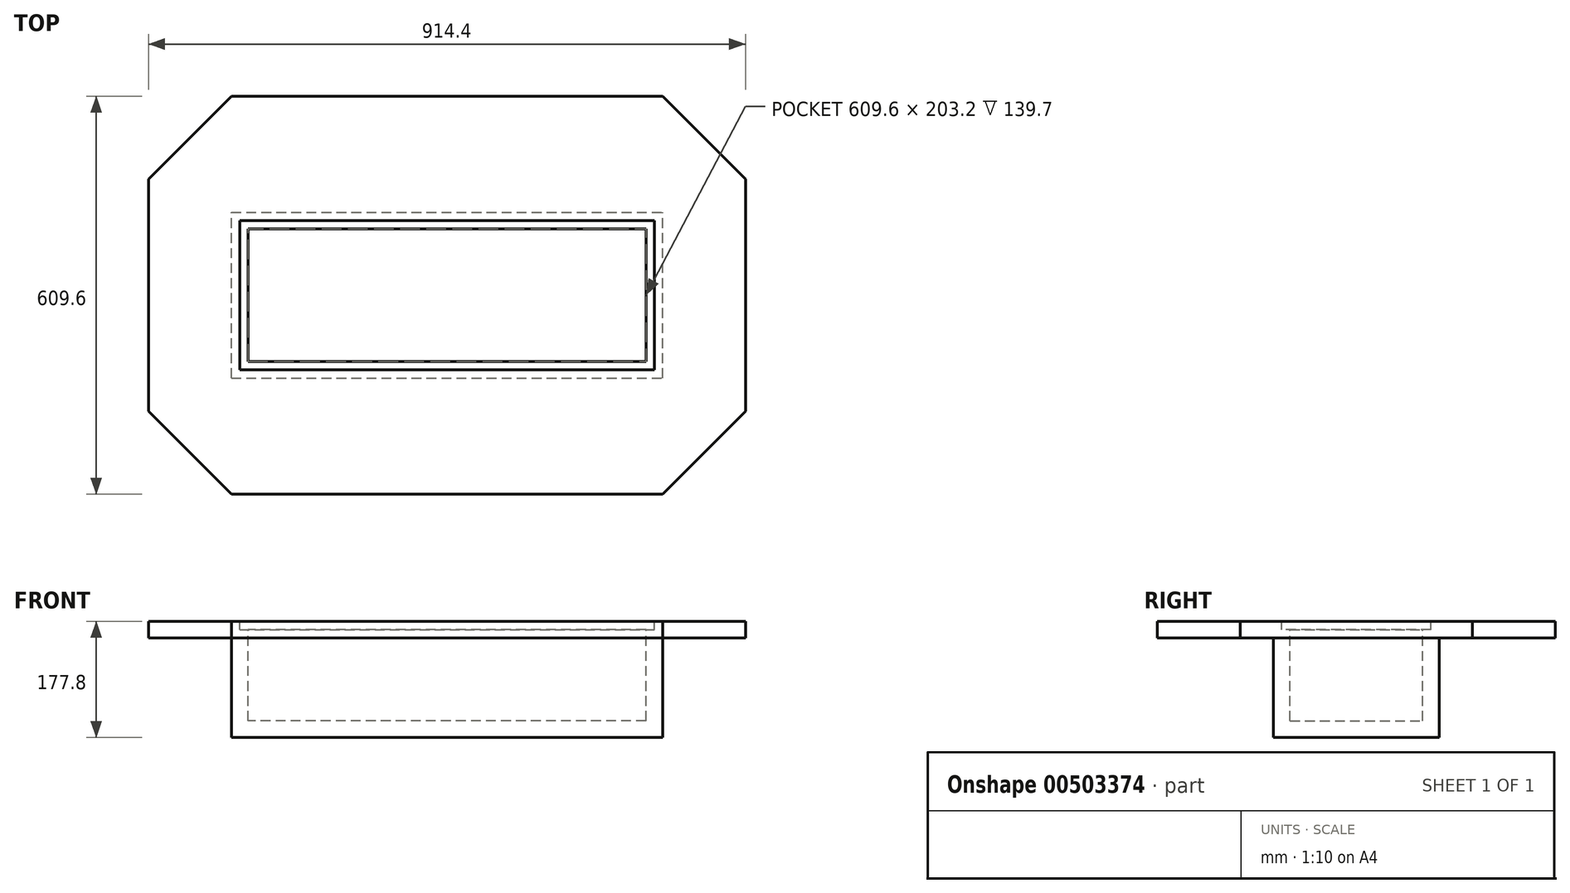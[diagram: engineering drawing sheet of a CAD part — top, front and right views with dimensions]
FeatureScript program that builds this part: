
annotation { "Feature Type Name" : "Feature", "Feature Type Description" : "" }
export const myFeature = defineFeature(function(context is Context, id is Id, definition is map)
    precondition{}
    {
        {
            var Q0;
            Q0=qCreatedBy(makeId("Top.planeOp"),FACE);
            var sketch = newSketch(context, id + "F0", { "sketchPlane" : qUnion([Q0])});
            skLineSegment(sketch, "E0.bottom", {"start": v(-457.2, 304.8) * mm, "end": v(457.2, 304.8) * mm});
            skLineSegment(sketch, "E0.top", {"start": v(-457.2, -304.8) * mm, "end": v(457.2, -304.8) * mm});
            skLineSegment(sketch, "E0.left", {"start": v(-457.2, 304.8) * mm, "end": v(-457.2, -304.8) * mm});
            skLineSegment(sketch, "E0.right", {"start": v(457.2, 304.8) * mm, "end": v(457.2, -304.8) * mm});
            skLineSegment(sketch, "E1", {"start": v(-457.2, 0) * mm, "end": v(457.2, 0) * mm, "construction": true});
            skSolve(sketch);
        }
        {
            var Q0;
            Q0 = qSketchRegion(id + "F0", true);
            extrude(context, id + "F1", {"entities" : qUnion([Q0]), "depth" : 25.4 * mm});
        }
        {
            var Q0;
            Q0=makeQuery(id+"F1.opExtrude","SWEPT_EDGE",EDGE,{"disambiguationData":[OSD([sQuery(id+"F0.wireOp",EDGE,"E0.top"),sQuery(id+"F0.wireOp",EDGE,"E0.left")])]});
            var Q1;
            Q1=makeQuery(id+"F1.opExtrude","SWEPT_EDGE",EDGE,{"disambiguationData":[OSD([sQuery(id+"F0.wireOp",EDGE,"E0.top"),sQuery(id+"F0.wireOp",EDGE,"E0.right")])]});
            var Q2;
            Q2=makeQuery(id+"F1.opExtrude","SWEPT_EDGE",EDGE,{"disambiguationData":[OSD([sQuery(id+"F0.wireOp",EDGE,"E0.bottom"),sQuery(id+"F0.wireOp",EDGE,"E0.right")])]});
            var Q3;
            Q3=makeQuery(id+"F1.opExtrude","SWEPT_EDGE",EDGE,{"disambiguationData":[OSD([sQuery(id+"F0.wireOp",EDGE,"E0.bottom"),sQuery(id+"F0.wireOp",EDGE,"E0.left")])]});
            chamfer(context, id + "F2", {"entities" : qUnion([Q0, Q1, Q2, Q3]), "width" : 127 * mm, "tangentPropagation" : true});
        }
        {
            var Q0;
            Q0=makeQuery(id+"F1.opExtrude","CAP_FACE",FACE,{"disambiguationData":[OSD([sQuery(id+"F0.wireOp",EDGE,"E0.bottom"),sQuery(id+"F0.wireOp",EDGE,"E0.top"),sQuery(id+"F0.wireOp",EDGE,"E0.left"),sQuery(id+"F0.wireOp",EDGE,"E0.right")])],"isStart":false});
            var sketch = newSketch(context, id + "F3", { "sketchPlane" : qUnion([Q0])});
            skLineSegment(sketch, "E2.bottom", {"start": v(-304.8, 101.6) * mm, "end": v(304.8, 101.6) * mm});
            skLineSegment(sketch, "E2.top", {"start": v(-304.8, -101.6) * mm, "end": v(304.8, -101.6) * mm});
            skLineSegment(sketch, "E2.left", {"start": v(-304.8, 101.6) * mm, "end": v(-304.8, -101.6) * mm});
            skLineSegment(sketch, "E2.right", {"start": v(304.8, 101.6) * mm, "end": v(304.8, -101.6) * mm});
            skLineSegment(sketch, "E3", {"start": v(-304.8, 0) * mm, "end": v(304.8, 0) * mm, "construction": true});
            skSolve(sketch);
        }
        {
            var Q0;
            Q0 = qSketchRegion(id + "F3", true);
            var Q1;
            Q1=makeQuery(id+"F1.opExtrude","CAP_FACE",FACE,{"disambiguationData":[OSD([sQuery(id+"F0.wireOp",EDGE,"E0.bottom"),sQuery(id+"F0.wireOp",EDGE,"E0.top"),sQuery(id+"F0.wireOp",EDGE,"E0.left"),sQuery(id+"F0.wireOp",EDGE,"E0.right")])],"isStart":true});
            extrude(context, id + "F4", {"entities" : qUnion([Q0]), "operationType" : NewBodyOperationType.REMOVE, "endBound" : BoundingType.UP_TO_SURFACE, "oppositeDirection" : true, "endBoundEntityFace" : qUnion([Q1]), "depth" : 25.4 * mm});
        }
        {
            var Q0;
            Q0=makeQuery(id+"F1.opExtrude","CAP_FACE",FACE,{"disambiguationData":[OSD([sQuery(id+"F0.wireOp",EDGE,"E0.bottom"),sQuery(id+"F0.wireOp",EDGE,"E0.top"),sQuery(id+"F0.wireOp",EDGE,"E0.left"),sQuery(id+"F0.wireOp",EDGE,"E0.right")])],"isStart":true});
            var sketch = newSketch(context, id + "F5", { "sketchPlane" : qUnion([Q0])});
            skLineSegment(sketch, "E4.bottom", {"start": v(-330.2, 127) * mm, "end": v(330.2, 127) * mm});
            skLineSegment(sketch, "E4.top", {"start": v(-330.2, -127) * mm, "end": v(330.2, -127) * mm});
            skLineSegment(sketch, "E4.left", {"start": v(-330.2, 127) * mm, "end": v(-330.2, -127) * mm});
            skLineSegment(sketch, "E4.right", {"start": v(330.2, 127) * mm, "end": v(330.2, -127) * mm});
            skLineSegment(sketch, "E5", {"start": v(-330.2, 0) * mm, "end": v(330.2, 0) * mm, "construction": true});
            skLineSegment(sketch, "E6.bottom", {"start": v(-304.8, 101.6) * mm, "end": v(304.8, 101.6) * mm});
            skLineSegment(sketch, "E6.top", {"start": v(-304.8, -101.6) * mm, "end": v(304.8, -101.6) * mm});
            skLineSegment(sketch, "E6.left", {"start": v(-304.8, 101.6) * mm, "end": v(-304.8, -101.6) * mm});
            skLineSegment(sketch, "E6.right", {"start": v(304.8, 101.6) * mm, "end": v(304.8, -101.6) * mm});
            skSolve(sketch);
        }
        {
            var Q0;
            Q0=makeQuery(id+"F5.imprint","IMPRINT",FACE,{"disambiguationData":[TD([[makeQuery(id+"F5.imprint","IMPRINT",EDGE,{"derivedFrom":sQuery(id+"F5.wireOp",EDGE,"E4.bottom")}),-1.0]])]});
            extrude(context, id + "F6", {"entities" : qUnion([Q0]), "operationType" : NewBodyOperationType.ADD, "depth" : 127 * mm});
        }
        {
            var Q0;
            Q0=makeQuery(id+"F6.opExtrude","CAP_FACE",FACE,{"disambiguationData":[OSD([sQuery(id+"F5.wireOp",EDGE,"E4.bottom"),sQuery(id+"F5.wireOp",EDGE,"E4.top"),sQuery(id+"F5.wireOp",EDGE,"E4.left"),sQuery(id+"F5.wireOp",EDGE,"E4.right"),sQuery(id+"F5.wireOp",EDGE,"E6.bottom"),sQuery(id+"F5.wireOp",EDGE,"E6.top"),sQuery(id+"F5.wireOp",EDGE,"E6.left"),sQuery(id+"F5.wireOp",EDGE,"E6.right")])],"isStart":false});
            var sketch = newSketch(context, id + "F7", { "sketchPlane" : qUnion([Q0])});
            skLineSegment(sketch, "E7.bottom", {"start": v(-330.2, 127) * mm, "end": v(330.2, 127) * mm});
            skLineSegment(sketch, "E7.top", {"start": v(-330.2, -127) * mm, "end": v(330.2, -127) * mm});
            skLineSegment(sketch, "E7.left", {"start": v(-330.2, 127) * mm, "end": v(-330.2, -127) * mm});
            skLineSegment(sketch, "E7.right", {"start": v(330.2, 127) * mm, "end": v(330.2, -127) * mm});
            skSolve(sketch);
        }
        {
            var Q0;
            Q0 = qSketchRegion(id + "F7", true);
            extrude(context, id + "F8", {"entities" : qUnion([Q0]), "operationType" : NewBodyOperationType.ADD, "depth" : 25.4 * mm});
        }
        {
            var Q0;
            Q0=makeQuery(id+"F1.opExtrude","CAP_FACE",FACE,{"disambiguationData":[OSD([sQuery(id+"F0.wireOp",EDGE,"E0.bottom"),sQuery(id+"F0.wireOp",EDGE,"E0.top"),sQuery(id+"F0.wireOp",EDGE,"E0.left"),sQuery(id+"F0.wireOp",EDGE,"E0.right")])],"isStart":false});
            var sketch = newSketch(context, id + "F9", { "sketchPlane" : qUnion([Q0])});
            skLineSegment(sketch, "E8.bottom", {"start": v(-317.5, 114.3) * mm, "end": v(317.5, 114.3) * mm});
            skLineSegment(sketch, "E8.top", {"start": v(-317.5, -114.3) * mm, "end": v(317.5, -114.3) * mm});
            skLineSegment(sketch, "E8.left", {"start": v(-317.5, 114.3) * mm, "end": v(-317.5, -114.3) * mm});
            skLineSegment(sketch, "E8.right", {"start": v(317.5, 114.3) * mm, "end": v(317.5, -114.3) * mm});
            skSolve(sketch);
        }
        {
            var Q0;
            Q0 = qSketchRegion(id + "F9", true);
            extrude(context, id + "F10", {"entities" : qUnion([Q0]), "operationType" : NewBodyOperationType.REMOVE, "oppositeDirection" : true, "depth" : 12.7 * mm});
        }
    });
